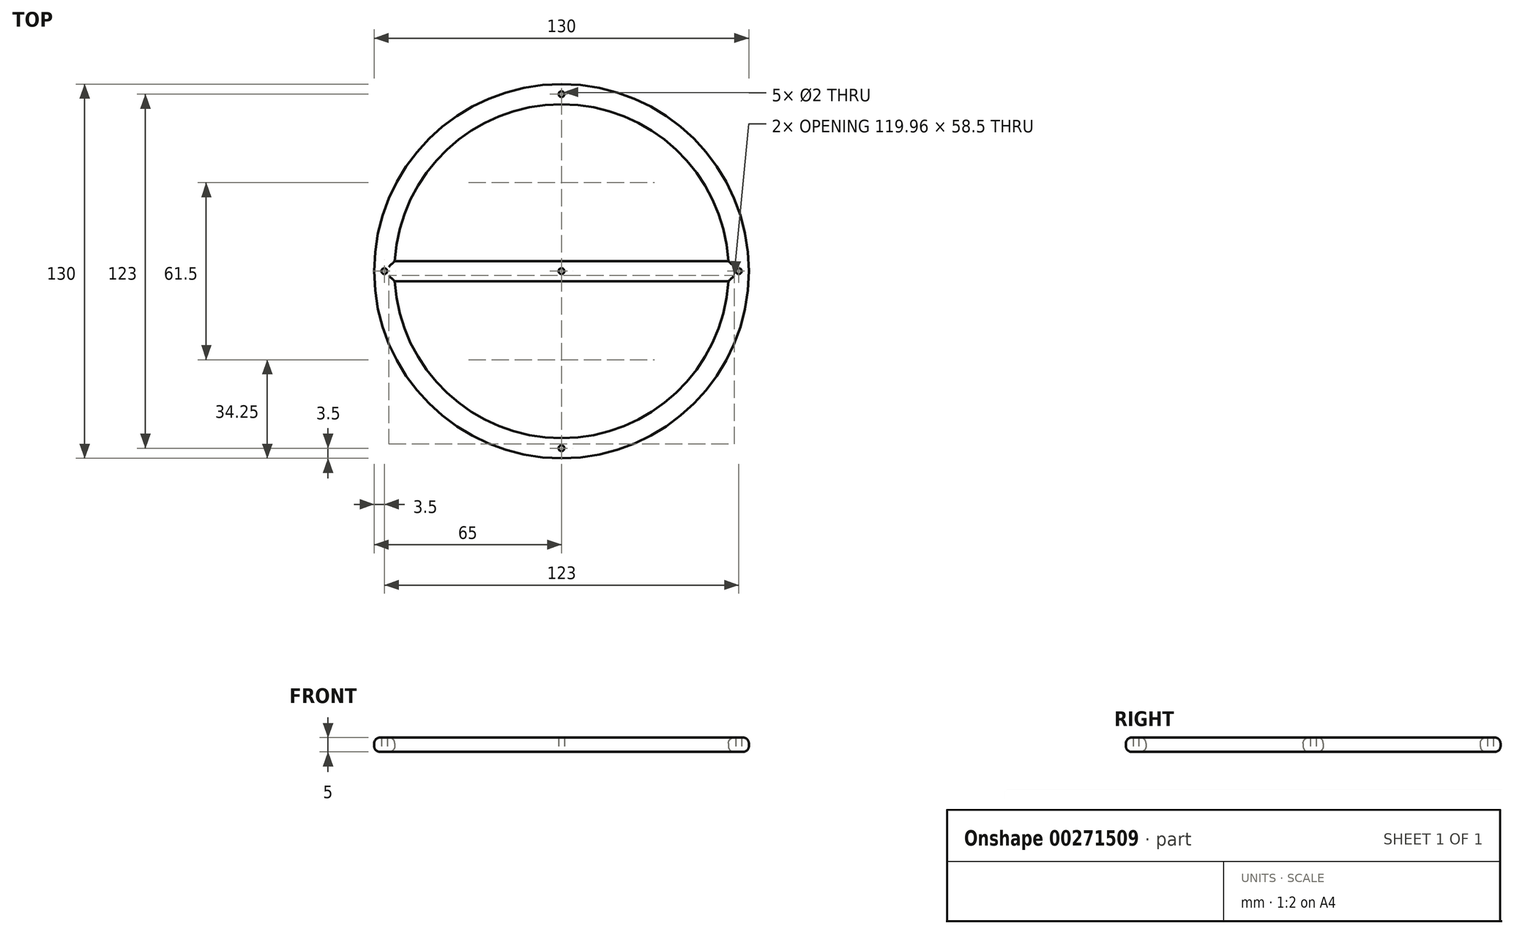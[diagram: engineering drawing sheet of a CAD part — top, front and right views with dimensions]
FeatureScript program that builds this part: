
annotation { "Feature Type Name" : "Feature", "Feature Type Description" : "" }
export const myFeature = defineFeature(function(context is Context, id is Id, definition is map)
    precondition{}
    {
        {
            var Q0;
            Q0=qCreatedBy(makeId("Top.planeOp"),FACE);
            var sketch = newSketch(context, id + "F0", { "sketchPlane" : qUnion([Q0])});
            skCircle(sketch, "E0", {"center": v(0, 0) * mm, "radius": 65 * mm});
            skCircle(sketch, "E1", {"center": v(0, 0) * mm, "radius": 58 * mm});
            skLineSegment(sketch, "E2", {"start": v(-57.9, 3.5) * mm, "end": v(57.9, 3.5) * mm});
            skLineSegment(sketch, "E3", {"start": v(-57.9, -3.5) * mm, "end": v(57.9, -3.5) * mm});
            skLineSegment(sketch, "E4", {"start": v(65, 0) * mm, "end": v(58, 0) * mm, "construction": true});
            skLineSegment(sketch, "E5", {"start": v(0, 65) * mm, "end": v(0, 58) * mm, "construction": true});
            skLineSegment(sketch, "E6.trimOffspring", {"start": v(0, 3.5) * mm, "end": v(0, -3.5) * mm, "construction": true});
            skLineSegment(sketch, "E7.trimOffspring", {"start": v(0, -58) * mm, "end": v(0, -65) * mm, "construction": true});
            skPoint(sketch, "E8.orphan", {"position": v(0, 71.84) * mm});
            skPoint(sketch, "E9.orphan", {"position": v(73.35, 0) * mm});
            skLineSegment(sketch, "E10.trimOffspring", {"start": v(-58, 0) * mm, "end": v(-65, 0) * mm, "construction": true});
            skPoint(sketch, "E11", {"position": v(0, -61.5) * mm});
            skPoint(sketch, "E12", {"position": v(-61.5, 0) * mm});
            skPoint(sketch, "E13", {"position": v(61.5, 0) * mm});
            skPoint(sketch, "E14", {"position": v(0, 61.5) * mm});
            skSolve(sketch);
        }
        {
            var Q0;
            Q0=makeQuery(id+"F0.imprint","IMPRINT",FACE,{"disambiguationData":[TD([[makeQuery(id+"F0.imprint","IMPRINT",EDGE,{"derivedFrom":sQuery(id+"F0.wireOp",EDGE,"E0")}),1.0]])]});
            var Q1;
            {var subQ0=sQuery(id+"F0.wireOp",EDGE,"E2");Q1=makeQuery(id+"F0.imprint","IMPRINT",FACE,{"disambiguationData":[TD([[makeQuery(id+"F0.imprint","IMPRINT",EDGE,{"derivedFrom":subQ0}),-1.0]])]});}
            extrude(context, id + "F1", {"entities" : qUnion([Q0, Q1]), "depth" : 5 * mm});
        }
        {
            var Q0;
            Q0=sQuery(id+"F0.wireOp",VERTEX,"E12");
            var Q1;
            Q1=sQuery(id+"F0.wireOp",VERTEX,"E1.center");
            var Q2;
            Q2=sQuery(id+"F0.wireOp",VERTEX,"E13");
            var Q3;
            Q3=sQuery(id+"F0.wireOp",VERTEX,"E11");
            var Q4;
            Q4=sQuery(id+"F0.wireOp",VERTEX,"E14");
            var Q5;
            Q5=makeQuery(id+"F1.opExtrude","SWEPT_BODY",BODY,{"disambiguationData":[OSD([sQuery(id+"F0.wireOp",EDGE,"E0"),sQuery(id+"F0.wireOp",EDGE,"E1"),sQuery(id+"F0.wireOp",EDGE,"E2"),sQuery(id+"F0.wireOp",EDGE,"E3")])]});
            hole(context, id + "F2", {"style" : HoleStyle.SIMPLE, "endStyle" : HoleEndStyle.THROUGH, "oppositeDirection" : true, "holeDiameter" : 2 * mm, "tappedDepth" : 12 * mm, "tapClearance" : 3, "locations" : qUnion([Q0, Q1, Q2, Q3, Q4]), "scope" : qUnion([Q5])});
        }
        {
            var Q0;
            {var subQ0=sQuery(id+"F0.wireOp",EDGE,"E2");var subQ1=sQuery(id+"F0.wireOp",EDGE,"E1");Q0=makeQuery(id+"F1.opExtrude","CAP_EDGE",EDGE,{"disambiguationData":[OSD([subQ1]),TDD([makeQuery(id+"F0.imprint","IMPRINT",EDGE,{"disambiguationData":[TD([[makeQuery(id+"F0.imprint","INTERSECT",VERTEX,{"disambiguationData":[OD(0.0)],"derivedFrom":[subQ1,subQ0]}),1.0]])],"derivedFrom":subQ1})])],"isStart":false});}
            var Q1;
            Q1=makeQuery(id+"F1.opExtrude","CAP_EDGE",EDGE,{"disambiguationData":[OSD([sQuery(id+"F0.wireOp",EDGE,"E0")])],"isStart":false});
            var Q2;
            Q2=makeQuery(id+"F1.opExtrude","CAP_EDGE",EDGE,{"disambiguationData":[OSD([sQuery(id+"F0.wireOp",EDGE,"E3")])],"isStart":false});
            var Q3;
            Q3=makeQuery(id+"F1.opExtrude","CAP_EDGE",EDGE,{"disambiguationData":[OSD([sQuery(id+"F0.wireOp",EDGE,"E2")])],"isStart":false});
            var Q4;
            {var subQ0=sQuery(id+"F0.wireOp",EDGE,"E3");var subQ1=sQuery(id+"F0.wireOp",EDGE,"E1");Q4=makeQuery(id+"F1.opExtrude","CAP_EDGE",EDGE,{"disambiguationData":[OSD([subQ1]),TDD([makeQuery(id+"F0.imprint","IMPRINT",EDGE,{"disambiguationData":[TD([[makeQuery(id+"F0.imprint","INTERSECT",VERTEX,{"disambiguationData":[OD(0.0)],"derivedFrom":[subQ1,subQ0]}),-1.0]])],"derivedFrom":subQ1})])],"isStart":false});}
            var Q5;
            Q5=makeQuery(id+"F1.opExtrude","CAP_EDGE",EDGE,{"disambiguationData":[OSD([sQuery(id+"F0.wireOp",EDGE,"E0")])],"isStart":true});
            var Q6;
            {var subQ0=sQuery(id+"F0.wireOp",EDGE,"E3");var subQ1=sQuery(id+"F0.wireOp",EDGE,"E1");Q6=makeQuery(id+"F1.opExtrude","CAP_EDGE",EDGE,{"disambiguationData":[OSD([subQ1]),TDD([makeQuery(id+"F0.imprint","IMPRINT",EDGE,{"disambiguationData":[TD([[makeQuery(id+"F0.imprint","INTERSECT",VERTEX,{"disambiguationData":[OD(0.0)],"derivedFrom":[subQ1,subQ0]}),-1.0]])],"derivedFrom":subQ1})])],"isStart":true});}
            var Q7;
            Q7=makeQuery(id+"F1.opExtrude","CAP_EDGE",EDGE,{"disambiguationData":[OSD([sQuery(id+"F0.wireOp",EDGE,"E3")])],"isStart":true});
            var Q8;
            {var subQ0=sQuery(id+"F0.wireOp",EDGE,"E2");var subQ1=sQuery(id+"F0.wireOp",EDGE,"E1");Q8=makeQuery(id+"F1.opExtrude","CAP_EDGE",EDGE,{"disambiguationData":[OSD([subQ1]),TDD([makeQuery(id+"F0.imprint","IMPRINT",EDGE,{"disambiguationData":[TD([[makeQuery(id+"F0.imprint","INTERSECT",VERTEX,{"disambiguationData":[OD(0.0)],"derivedFrom":[subQ1,subQ0]}),1.0]])],"derivedFrom":subQ1})])],"isStart":true});}
            var Q9;
            Q9=makeQuery(id+"F1.opExtrude","CAP_EDGE",EDGE,{"disambiguationData":[OSD([sQuery(id+"F0.wireOp",EDGE,"E2")])],"isStart":true});
            fillet(context, id + "F3", {"entities" : qUnion([Q0, Q1, Q2, Q3, Q4, Q5, Q6, Q7, Q8, Q9]), "radius" : 2 * mm, "tangentPropagation" : true, "allowEdgeOverflow" : false});
        }
    });
